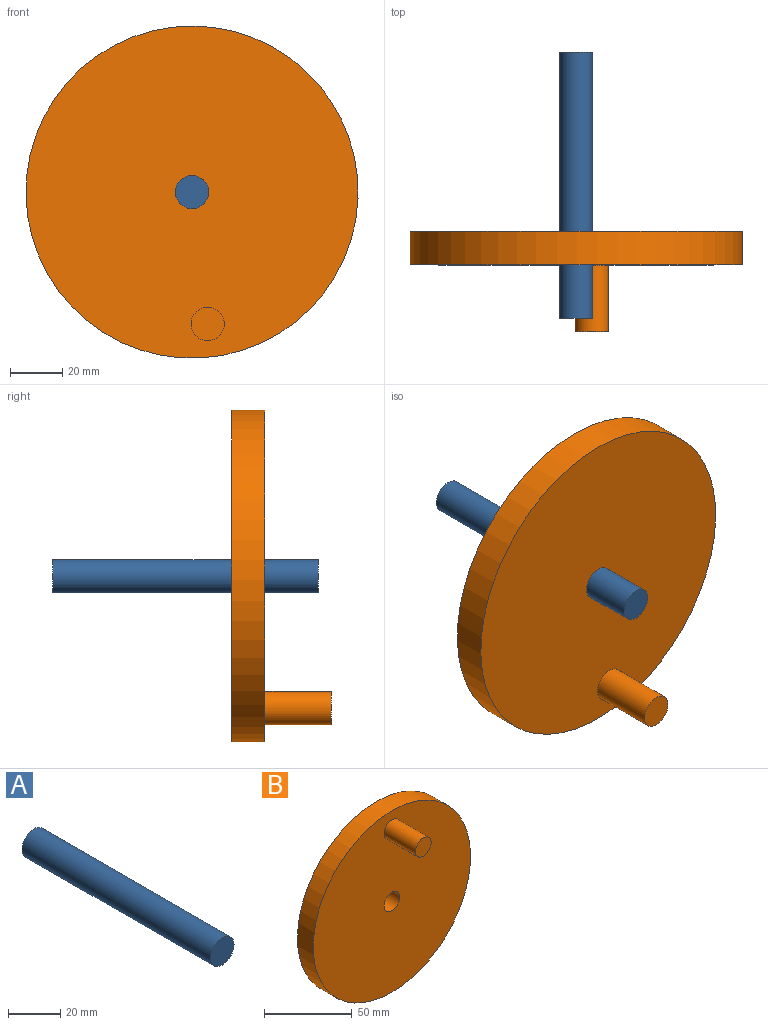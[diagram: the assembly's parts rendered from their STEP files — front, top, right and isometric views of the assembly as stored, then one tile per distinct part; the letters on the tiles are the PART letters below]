
ASSEMBLY  parts=2 mates=1
PART A: 3 faces, bbox 12.7x101.6x12.7 mm
  f0: cylinder r=6.35mm len=101.6mm, axis (0,1,0), area 4053.7mm2, adj f1,f2
  f1: plane 12.7x12.7mm, normal (0,-1,0), area 126.7mm2, adj f0
  f2: plane 12.7x12.7mm, normal (0,1,0), area 126.7mm2, adj f0
PART B: 6 faces, bbox 127x38.1x127 mm
  f0: cylinder r=63.5mm len=127mm, axis (0,1,0), area 5067.1mm2, adj f1,f2
  f1: plane 127x127mm, normal (0,-1,0), area 12414.3mm2, adj f0,f3,f5
  f2: plane 127x127mm, normal (0,1,0), area 12541mm2, adj f0,f5
  f3: cylinder r=6.35mm len=25.4mm, axis (0,1,0), area 1013.4mm2, adj f1,f4
  f4: plane 12.7x12.7mm, normal (0,-1,0), area 126.7mm2, adj f3
  f5: cylinder r=6.35mm len=12.7mm, axis (0,1,0), area 506.7mm2, adj f1,f2
PLACE A t=(-81.52,4.17,-8.37)mm
PLACE B rot(axis=(0,1,0),173.3deg) t=(-81.52,-64.31,-8.37)mm
MATE cylindrical B.f5 <-> A.f0  axis (0,1,0) through (-81.52,-77.01,-8.37)mm
